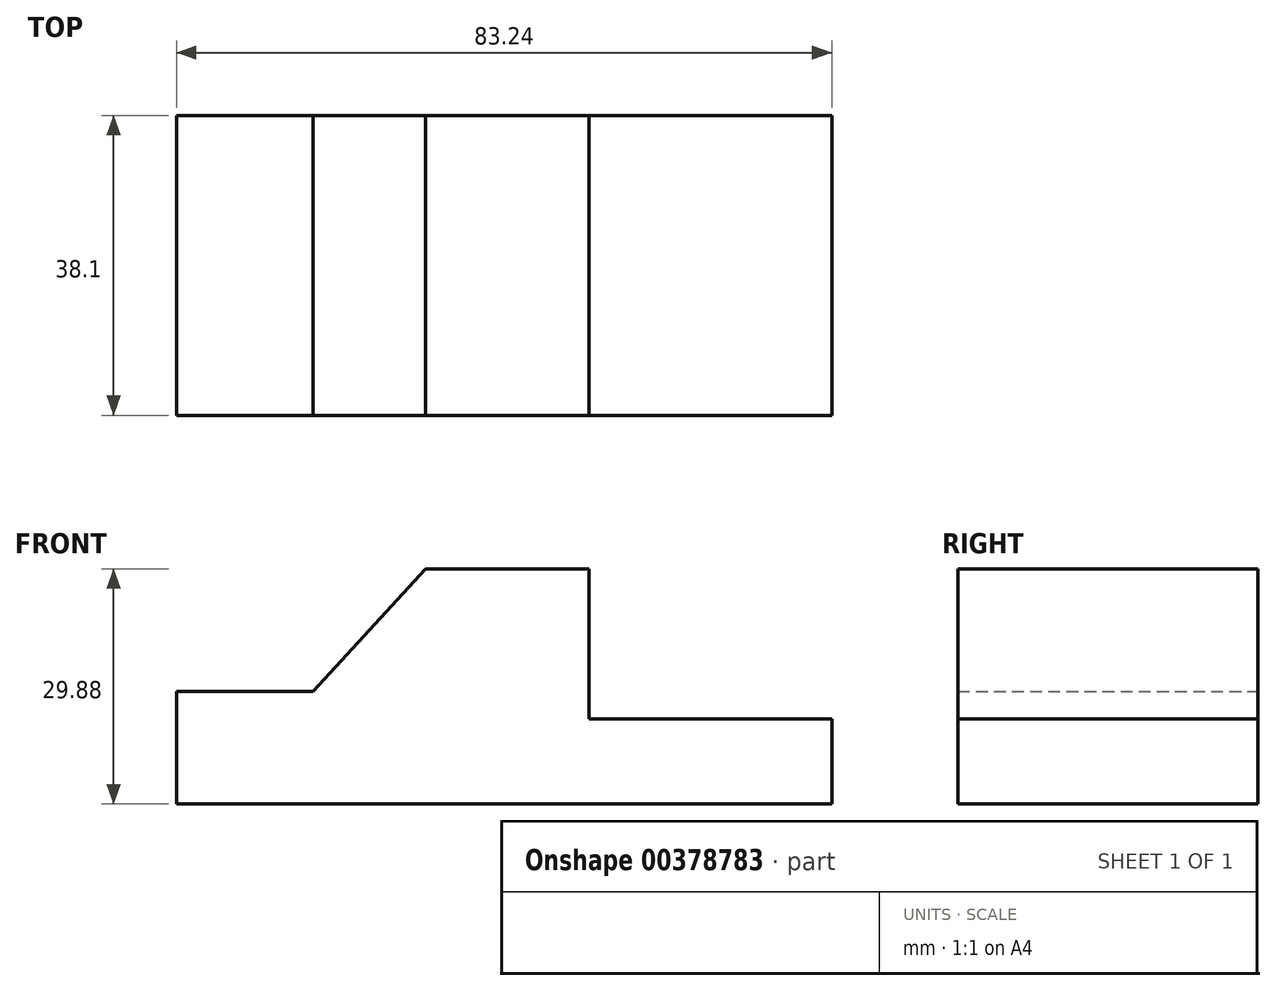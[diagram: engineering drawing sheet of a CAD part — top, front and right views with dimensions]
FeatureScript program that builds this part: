
annotation { "Feature Type Name" : "Feature", "Feature Type Description" : "" }
export const myFeature = defineFeature(function(context is Context, id is Id, definition is map)
    precondition{}
    {
        {
            var Q0;
            Q0=qCreatedBy(makeId("Front.planeOp"),FACE);
            var sketch = newSketch(context, id + "F0", { "sketchPlane" : qUnion([Q0])});
            skLineSegment(sketch, "E0", {"start": v(-31.61, 35.08) * mm, "end": v(-31.61, 49.37) * mm});
            skLineSegment(sketch, "E1", {"start": v(-31.61, 49.37) * mm, "end": v(-14.3, 49.37) * mm});
            skLineSegment(sketch, "E2", {"start": v(-14.3, 49.37) * mm, "end": v(0, 64.96) * mm});
            skLineSegment(sketch, "E3", {"start": v(0, 64.96) * mm, "end": v(20.79, 64.96) * mm});
            skLineSegment(sketch, "E4", {"start": v(20.79, 64.96) * mm, "end": v(20.79, 45.9) * mm});
            skLineSegment(sketch, "E5", {"start": v(20.79, 45.9) * mm, "end": v(51.63, 45.9) * mm});
            skLineSegment(sketch, "E6", {"start": v(51.63, 45.9) * mm, "end": v(51.63, 35.08) * mm});
            skLineSegment(sketch, "E7", {"start": v(51.63, 35.08) * mm, "end": v(-31.61, 35.08) * mm});
            skSolve(sketch);
        }
        {
            var Q0;
            Q0 = qSketchRegion(id + "F0", true);
            extrude(context, id + "F1", {"entities" : qUnion([Q0]), "depth" : 38.1 * mm});
        }
    });
